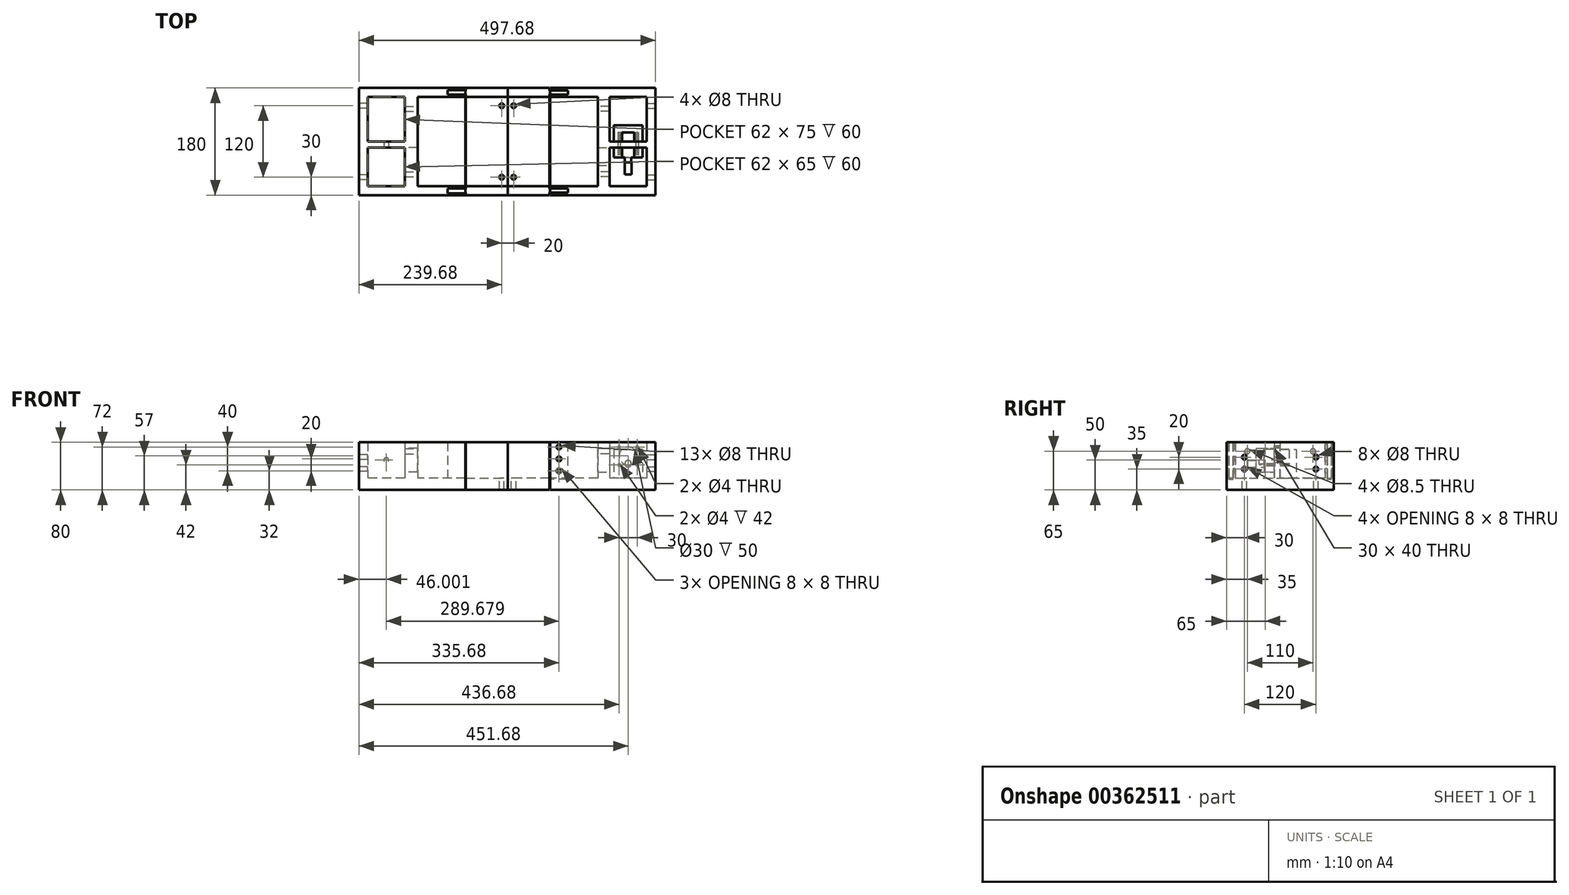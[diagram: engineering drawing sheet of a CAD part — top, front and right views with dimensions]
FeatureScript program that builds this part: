
annotation { "Feature Type Name" : "Feature", "Feature Type Description" : "" }
export const myFeature = defineFeature(function(context is Context, id is Id, definition is map)
    precondition{}
    {
        {
            var Q0;
            Q0=qCreatedBy(makeId("Top.planeOp"),FACE);
            var sketch = newSketch(context, id + "F0", { "sketchPlane" : qUnion([Q0])});
            skLineSegment(sketch, "E0.bottom", {"start": v(24, -27) * mm, "end": v(-24, -27) * mm});
            skLineSegment(sketch, "E0.top", {"start": v(24, 27) * mm, "end": v(-24, 27) * mm});
            skLineSegment(sketch, "E0.left", {"start": v(24, -27) * mm, "end": v(24, 27) * mm});
            skLineSegment(sketch, "E0.right", {"start": v(-24, -27) * mm, "end": v(-24, 27) * mm});
            skPoint(sketch, "E0.middle", {"position": v(0, 0) * mm});
            skSolve(sketch);
        }
        {
            var Q0;
            Q0=makeQuery(id+"F0.imprint","IMPRINT",FACE,{"disambiguationData":[TD([[makeQuery(id+"F0.imprint","IMPRINT",EDGE,{"derivedFrom":sQuery(id+"F0.wireOp",EDGE,"E0.bottom")}),-1.0]])]});
            extrude(context, id + "F1", {"entities" : qUnion([Q0]), "depth" : 48 * mm});
        }
        {
            var Q0;
            Q0=makeQuery(id+"F1.opExtrude","SWEPT_FACE",FACE,{"disambiguationData":[OSD([sQuery(id+"F0.wireOp",EDGE,"E0.bottom")])]});
            var sketch = newSketch(context, id + "F2", { "sketchPlane" : qUnion([Q0])});
            skCircle(sketch, "E1", {"center": v(0, 24) * mm, "radius": 5.5 * mm});
            skPoint(sketch, "E1.centerSnap0", {"position": v(-24, 24) * mm});
            skSolve(sketch);
        }
        {
            var Q0;
            Q0=makeQuery(id+"F2.imprint","IMPRINT",FACE,{"disambiguationData":[TD([[makeQuery(id+"F2.imprint","IMPRINT",EDGE,{"derivedFrom":sQuery(id+"F2.wireOp",EDGE,"E1")}),1.0]])]});
            extrude(context, id + "F3", {"entities" : qUnion([Q0]), "operationType" : NewBodyOperationType.ADD, "depth" : 28 * mm});
        }
        {
            var Q0;
            Q0=qCreatedBy(makeId("Top.planeOp"),FACE);
            var sketch = newSketch(context, id + "F4", { "sketchPlane" : qUnion([Q0])});
            skLineSegment(sketch, "E2.bottom", {"start": v(31, -75) * mm, "end": v(-31, -75) * mm});
            skLineSegment(sketch, "E2.top", {"start": v(31, 75) * mm, "end": v(-31, 75) * mm});
            skLineSegment(sketch, "E2.left", {"start": v(31, -75) * mm, "end": v(31, 75) * mm});
            skLineSegment(sketch, "E2.right", {"start": v(-31, -75) * mm, "end": v(-31, 75) * mm});
            skPoint(sketch, "E2.middle", {"position": v(0, 0) * mm});
            skLineSegment(sketch, "E3.bottom", {"start": v(-31, -75) * mm, "end": v(-51, -75) * mm});
            skLineSegment(sketch, "E3.top", {"start": v(-31, 75) * mm, "end": v(-51, 75) * mm});
            skLineSegment(sketch, "E3.right", {"start": v(-51, -75) * mm, "end": v(-51, 75) * mm});
            skLineSegment(sketch, "E4.bottom", {"start": v(-51, -75) * mm, "end": v(-51, -75) * mm});
            skLineSegment(sketch, "E4.top", {"start": v(-51, 75) * mm, "end": v(-51, 75) * mm});
            skLineSegment(sketch, "E5.bottom", {"start": v(-51, -75) * mm, "end": v(-131, -75) * mm});
            skLineSegment(sketch, "E5.left", {"start": v(-51, -75) * mm, "end": v(-51, 74.37) * mm});
            skLineSegment(sketch, "E6", {"start": v(-51, 75) * mm, "end": v(-131, 75) * mm});
            skLineSegment(sketch, "E7", {"start": v(-131, 75) * mm, "end": v(-131, -75) * mm});
            skLineSegment(sketch, "E8", {"start": v(-131, 75) * mm, "end": v(-131, 90) * mm});
            skLineSegment(sketch, "E9", {"start": v(-131, 90) * mm, "end": v(46, 90) * mm});
            skLineSegment(sketch, "E10", {"start": v(46, 90) * mm, "end": v(46, -90) * mm});
            skLineSegment(sketch, "E11", {"start": v(46, -90) * mm, "end": v(-131, -90) * mm});
            skLineSegment(sketch, "E12", {"start": v(-131, -90) * mm, "end": v(-131, -75) * mm});
            skLineSegment(sketch, "E13.bottom", {"start": v(31, 0) * mm, "end": v(-31, 0) * mm});
            skLineSegment(sketch, "E13.top", {"start": v(31, -10) * mm, "end": v(-31, -10) * mm});
            skLineSegment(sketch, "E13.left", {"start": v(31, 0) * mm, "end": v(31, -10) * mm});
            skLineSegment(sketch, "E13.right", {"start": v(-31, 0) * mm, "end": v(-31, -10) * mm});
            skSolve(sketch);
        }
        {
            var Q0;
            Q0=makeQuery(id+"F4.imprint","IMPRINT",FACE,{"disambiguationData":[TD([[makeQuery(id+"F4.imprint","IMPRINT",EDGE,{"derivedFrom":sQuery(id+"F4.wireOp",EDGE,"E2.bottom")}),1.0]])]});
            var Q1;
            Q1=makeQuery(id+"F4.imprint","IMPRINT",FACE,{"disambiguationData":[TD([[makeQuery(id+"F4.imprint","IMPRINT",EDGE,{"derivedFrom":sQuery(id+"F4.wireOp",EDGE,"E3.bottom")}),-1.0]])]});
            var Q2;
            Q2=makeQuery(id+"F4.imprint","IMPRINT",FACE,{"disambiguationData":[TD([[makeQuery(id+"F4.imprint","IMPRINT",EDGE,{"derivedFrom":sQuery(id+"F4.wireOp",EDGE,"E13.bottom")}),1.0]])]});
            extrude(context, id + "F5", {"entities" : qUnion([Q0, Q1, Q2]), "depth" : 60 * mm});
        }
        {
            var Q0;
            Q0=makeQuery(id+"F5.opExtrude","CAP_FACE",FACE,{"disambiguationData":[OSD([sQuery(id+"F4.wireOp",EDGE,"E2.bottom"),sQuery(id+"F4.wireOp",EDGE,"E2.top"),sQuery(id+"F4.wireOp",EDGE,"E2.left"),sQuery(id+"F4.wireOp",EDGE,"E2.right"),sQuery(id+"F4.wireOp",EDGE,"E3.right"),sQuery(id+"F4.wireOp",EDGE,"E5.bottom"),sQuery(id+"F4.wireOp",EDGE,"E5.left"),sQuery(id+"F4.wireOp",EDGE,"E6"),sQuery(id+"F4.wireOp",EDGE,"E8"),sQuery(id+"F4.wireOp",EDGE,"E9"),sQuery(id+"F4.wireOp",EDGE,"E10"),sQuery(id+"F4.wireOp",EDGE,"E11"),sQuery(id+"F4.wireOp",EDGE,"E12")])],"isStart":true});
            var sketch = newSketch(context, id + "F6", { "sketchPlane" : qUnion([Q0])});
            skLineSegment(sketch, "E14.bottom", {"start": v(46, 90) * mm, "end": v(-131, 90) * mm});
            skLineSegment(sketch, "E14.top", {"start": v(46, -90) * mm, "end": v(-131, -90) * mm});
            skLineSegment(sketch, "E14.left", {"start": v(46, 90) * mm, "end": v(46, -90) * mm});
            skLineSegment(sketch, "E14.right", {"start": v(-131, 90) * mm, "end": v(-131, -90) * mm});
            skSolve(sketch);
        }
        {
            var Q0;
            Q0=makeQuery(id+"F6.imprint","IMPRINT",FACE,{"disambiguationData":[TD([[makeQuery(id+"F6.imprint","IMPRINT",EDGE,{"derivedFrom":makeQuery(id+"F5.opExtrude","CAP_EDGE",EDGE,{"disambiguationData":[OSD([sQuery(id+"F4.wireOp",EDGE,"E2.bottom")])],"isStart":true})}),1.0]])]});
            var Q1;
            {var subQ1=makeQuery(id+"F5.opExtrude","CAP_EDGE",EDGE,{"disambiguationData":[OSD([sQuery(id+"F4.wireOp",EDGE,"E5.bottom")])],"isStart":true});Q1=makeQuery(id+"F6.imprint","IMPRINT",FACE,{"disambiguationData":[TD([[makeQuery(id+"F6.imprint","IMPRINT",EDGE,{"derivedFrom":subQ1}),1.0]])]});}
            var Q2;
            {var subQ10=sQuery(id+"F6.wireOp",EDGE,"E14.bottom");Q2=makeQuery(id+"F6.imprint","IMPRINT",FACE,{"disambiguationData":[TD([[makeQuery(id+"F6.imprint","IMPRINT",EDGE,{"derivedFrom":subQ10}),1.0]])]});}
            var Q3;
            {var subQ0=sQuery(id+"F4.wireOp",EDGE,"E2.top");Q3=makeQuery(id+"F6.imprint","IMPRINT",FACE,{"disambiguationData":[TD([[makeQuery(id+"F6.imprint","IMPRINT",EDGE,{"derivedFrom":makeQuery(id+"F5.opExtrude","CAP_EDGE",EDGE,{"disambiguationData":[OSD([subQ0])],"isStart":true})}),-1.0]])]});}
            extrude(context, id + "F7", {"entities" : qUnion([Q0, Q1, Q2, Q3]), "operationType" : NewBodyOperationType.ADD, "depth" : 20 * mm});
        }
        {
            var Q0;
            Q0=makeQuery(id+"F5.opExtrude","SWEPT_FACE",FACE,{"disambiguationData":[OSD([sQuery(id+"F4.wireOp",EDGE,"E2.right")])]});
            var sketch = newSketch(context, id + "F8", { "sketchPlane" : qUnion([Q0])});
            skLineSegment(sketch, "E15.bottom", {"start": v(-40, 50) * mm, "end": v(-10, 50) * mm});
            skLineSegment(sketch, "E15.top", {"start": v(-40, 10) * mm, "end": v(-10, 10) * mm});
            skLineSegment(sketch, "E15.left", {"start": v(-40, 50) * mm, "end": v(-40, 10) * mm});
            skLineSegment(sketch, "E15.right", {"start": v(-10, 50) * mm, "end": v(-10, 10) * mm});
            skSolve(sketch);
        }
        {
            var Q0;
            Q0 = qSketchRegion(id + "F8", true);
            extrude(context, id + "F9", {"entities" : qUnion([Q0]), "operationType" : NewBodyOperationType.REMOVE, "oppositeDirection" : true, "depth" : 25 * mm});
        }
        {
            var Q0;
            Q0=makeQuery(id+"F9.boolean.opBoolean","MERGE",FACE,{"derivedFrom":[makeQuery(id+"F5.opExtrude","SWEPT_FACE",FACE,{"disambiguationData":[OSD([sQuery(id+"F4.wireOp",EDGE,"E13.top")])]}),makeQuery(id+"F9.opExtrude","SWEPT_FACE",FACE,{"disambiguationData":[OSD([sQuery(id+"F8.wireOp",EDGE,"E15.right")])]})]});
            var sketch = newSketch(context, id + "F10", { "sketchPlane" : qUnion([Q0])});
            skLineSegment(sketch, "E16", {"start": v(0, 60) * mm, "end": v(0, 52) * mm, "construction": true});
            skLineSegment(sketch, "E17", {"start": v(0, 52) * mm, "end": v(15, 52) * mm, "construction": true});
            skLineSegment(sketch, "E18", {"start": v(0, 52) * mm, "end": v(-15, 52) * mm, "construction": true});
            skCircle(sketch, "E19", {"center": v(-15, 52) * mm, "radius": 2 * mm});
            skCircle(sketch, "E20", {"center": v(15, 52) * mm, "radius": 2 * mm});
            skLineSegment(sketch, "E21", {"start": v(-15, 52) * mm, "end": v(-15, 22) * mm, "construction": true});
            skCircle(sketch, "E22", {"center": v(-15, 22) * mm, "radius": 2 * mm});
            skCircle(sketch, "E23", {"center": v(15, 22) * mm, "radius": 2 * mm});
            skLineSegment(sketch, "E24", {"start": v(15, 52) * mm, "end": v(-15, 22) * mm, "construction": true});
            skLineSegment(sketch, "E25", {"start": v(-15, 52) * mm, "end": v(15, 22) * mm, "construction": true});
            skCircle(sketch, "E26", {"center": v(0, 37) * mm, "radius": 15 * mm});
            skSolve(sketch);
        }
        {
            var Q0;
            Q0 = qSketchRegion(id + "F10", true);
            extrude(context, id + "F11", {"entities" : qUnion([Q0]), "operationType" : NewBodyOperationType.REMOVE, "oppositeDirection" : true, "depth" : 25 * mm, "hasSecondDirection" : true, "secondDirectionOppositeDirection" : false, "secondDirectionDepth" : 25 * mm});
        }
        {
            var Q0;
            Q0=makeQuery(id+"F7.boolean.opBoolean","MERGE",FACE,{"derivedFrom":[makeQuery(id+"F5.opExtrude","SWEPT_FACE",FACE,{"disambiguationData":[OSD([sQuery(id+"F4.wireOp",EDGE,"E11")])]}),makeQuery(id+"F7.opExtrude","SWEPT_FACE",FACE,{"disambiguationData":[OSD([sQuery(id+"F6.wireOp",EDGE,"E14.bottom")])]})]});
            var sketch = newSketch(context, id + "F12", { "sketchPlane" : qUnion([Q0])});
            skLineSegment(sketch, "E27", {"start": v(-116, 60) * mm, "end": v(-116, 52) * mm, "construction": true});
            skCircle(sketch, "E28", {"center": v(-116, 52) * mm, "radius": 4 * mm});
            skLineSegment(sketch, "E29", {"start": v(-116, 52) * mm, "end": v(-116, 32) * mm, "construction": true});
            skLineSegment(sketch, "E30", {"start": v(-116, 32) * mm, "end": v(-116, 12) * mm, "construction": true});
            skCircle(sketch, "E31", {"center": v(-116, 32) * mm, "radius": 4 * mm});
            skCircle(sketch, "E32", {"center": v(-116, 12) * mm, "radius": 4 * mm});
            skSolve(sketch);
        }
        {
            var Q0;
            Q0=makeQuery(id+"F7.boolean.opBoolean","MERGE",FACE,{"derivedFrom":[makeQuery(id+"F5.opExtrude","SWEPT_FACE",FACE,{"disambiguationData":[OSD([sQuery(id+"F4.wireOp",EDGE,"E10")])]}),makeQuery(id+"F7.opExtrude","SWEPT_FACE",FACE,{"disambiguationData":[OSD([sQuery(id+"F6.wireOp",EDGE,"E14.left")])]})]});
            var sketch = newSketch(context, id + "F13", { "sketchPlane" : qUnion([Q0])});
            skLineSegment(sketch, "E33", {"start": v(-90, 0) * mm, "end": v(-75, 0) * mm, "construction": true});
            skLineSegment(sketch, "E34", {"start": v(-75, 0) * mm, "end": v(-60, 0) * mm, "construction": true});
            skLineSegment(sketch, "E35", {"start": v(-60, 0) * mm, "end": v(-60, 15) * mm, "construction": true});
            skCircle(sketch, "E36", {"center": v(-60, 15) * mm, "radius": 4 * mm});
            skLineSegment(sketch, "E37", {"start": v(-60, 15) * mm, "end": v(-60, 35) * mm, "construction": true});
            skCircle(sketch, "E38", {"center": v(-60, 35) * mm, "radius": 4 * mm});
            skLineSegment(sketch, "E39", {"start": v(-60, 15) * mm, "end": v(60, 15) * mm, "construction": true});
            skLineSegment(sketch, "E40", {"start": v(90, 15) * mm, "end": v(60, 15) * mm, "construction": true});
            skCircle(sketch, "E41", {"center": v(60, 15) * mm, "radius": 4 * mm});
            skCircle(sketch, "E42", {"center": v(60, 35) * mm, "radius": 4 * mm});
            skSolve(sketch);
        }
        {
            var Q0;
            Q0=makeQuery(id+"F5.opExtrude","CAP_FACE",FACE,{"disambiguationData":[OSD([sQuery(id+"F4.wireOp",EDGE,"E2.bottom"),sQuery(id+"F4.wireOp",EDGE,"E2.top"),sQuery(id+"F4.wireOp",EDGE,"E2.left"),sQuery(id+"F4.wireOp",EDGE,"E2.right"),sQuery(id+"F4.wireOp",EDGE,"E3.right"),sQuery(id+"F4.wireOp",EDGE,"E5.bottom"),sQuery(id+"F4.wireOp",EDGE,"E5.left"),sQuery(id+"F4.wireOp",EDGE,"E6"),sQuery(id+"F4.wireOp",EDGE,"E8"),sQuery(id+"F4.wireOp",EDGE,"E9"),sQuery(id+"F4.wireOp",EDGE,"E10"),sQuery(id+"F4.wireOp",EDGE,"E11"),sQuery(id+"F4.wireOp",EDGE,"E12"),sQuery(id+"F4.wireOp",EDGE,"E13.bottom"),sQuery(id+"F4.wireOp",EDGE,"E13.top")])],"isStart":false});
            var sketch = newSketch(context, id + "F14", { "sketchPlane" : qUnion([Q0])});
            skLineSegment(sketch, "E43", {"start": v(-131, -82.5) * mm, "end": v(-101, -82.5) * mm, "construction": true});
            skPoint(sketch, "E43.endSnap0", {"position": v(-131, -82.5) * mm});
            skLineSegment(sketch, "E44", {"start": v(-101, -82.5) * mm, "end": v(-101, -79) * mm, "construction": true});
            skLineSegment(sketch, "E45", {"start": v(-101, -82.5) * mm, "end": v(-101, -86) * mm, "construction": true});
            skLineSegment(sketch, "E46.bottom", {"start": v(-101, -86) * mm, "end": v(-131, -86) * mm});
            skLineSegment(sketch, "E46.top", {"start": v(-101, -79) * mm, "end": v(-131, -79) * mm});
            skLineSegment(sketch, "E46.left", {"start": v(-101, -86) * mm, "end": v(-101, -79) * mm});
            skLineSegment(sketch, "E46.right", {"start": v(-131, -86) * mm, "end": v(-131, -79) * mm});
            skLineSegment(sketch, "E47.MirrorCS", {"start": v(-101, 86) * mm, "end": v(-131, 86) * mm});
            skLineSegment(sketch, "E48.MirrorCS", {"start": v(-101, 86) * mm, "end": v(-101, 79) * mm});
            skLineSegment(sketch, "E49.MirrorCS", {"start": v(-101, 82.5) * mm, "end": v(-101, 86) * mm, "construction": true});
            skLineSegment(sketch, "E50.MirrorCS", {"start": v(-101, 82.5) * mm, "end": v(-101, 79) * mm, "construction": true});
            skLineSegment(sketch, "E51.MirrorCS", {"start": v(-131, 86) * mm, "end": v(-131, 79) * mm});
            skLineSegment(sketch, "E52.MirrorCS", {"start": v(-101, 79) * mm, "end": v(-131, 79) * mm});
            skLineSegment(sketch, "E53.MirrorCS", {"start": v(-131, 82.5) * mm, "end": v(-101, 82.5) * mm, "construction": true});
            skPoint(sketch, "E54.MirrorP", {"position": v(-131, 82.5) * mm});
            skSolve(sketch);
        }
        {
            var Q0;
            Q0=makeQuery(id+"F13.imprint","IMPRINT",FACE,{"disambiguationData":[TD([[makeQuery(id+"F13.imprint","IMPRINT",EDGE,{"derivedFrom":sQuery(id+"F13.wireOp",EDGE,"E36")}),1.0]])]});
            var Q1;
            Q1=makeQuery(id+"F13.imprint","IMPRINT",FACE,{"disambiguationData":[TD([[makeQuery(id+"F13.imprint","IMPRINT",EDGE,{"derivedFrom":sQuery(id+"F13.wireOp",EDGE,"E38")}),1.0]])]});
            var Q2;
            Q2=makeQuery(id+"F13.imprint","IMPRINT",FACE,{"disambiguationData":[TD([[makeQuery(id+"F13.imprint","IMPRINT",EDGE,{"derivedFrom":sQuery(id+"F13.wireOp",EDGE,"E42")}),1.0]])]});
            var Q3;
            Q3=makeQuery(id+"F13.imprint","IMPRINT",FACE,{"disambiguationData":[TD([[makeQuery(id+"F13.imprint","IMPRINT",EDGE,{"derivedFrom":sQuery(id+"F13.wireOp",EDGE,"E41")}),1.0]])]});
            extrude(context, id + "F15", {"entities" : qUnion([Q0, Q1, Q2, Q3]), "operationType" : NewBodyOperationType.REMOVE, "oppositeDirection" : true, "depth" : 25 * mm});
        }
        {
            var Q0;
            Q0=qCreatedBy(makeId("Top.planeOp"),FACE);
            var sketch = newSketch(context, id + "F16", { "sketchPlane" : qUnion([Q0])});
            skLineSegment(sketch, "E55.bottom", {"start": v(-132, -90) * mm, "end": v(-202, -90) * mm});
            skLineSegment(sketch, "E56", {"start": v(-202, -90) * mm, "end": v(-202, -75) * mm});
            skLineSegment(sketch, "E57", {"start": v(-132, -75) * mm, "end": v(-202, -75) * mm});
            skLineSegment(sketch, "E58", {"start": v(-132, -90) * mm, "end": v(-132, -85.8) * mm});
            skLineSegment(sketch, "E59", {"start": v(-132, -85.8) * mm, "end": v(-103, -85.8) * mm});
            skLineSegment(sketch, "E60", {"start": v(-132, -75) * mm, "end": v(-132, -79.2) * mm});
            skLineSegment(sketch, "E61", {"start": v(-132, -79.2) * mm, "end": v(-103, -79.2) * mm});
            skLineSegment(sketch, "E62", {"start": v(-103, -79.2) * mm, "end": v(-103, -85.8) * mm});
            skSolve(sketch);
        }
        {
            var Q0;
            Q0=makeQuery(id+"F16.imprint","IMPRINT",FACE,{"disambiguationData":[TD([[makeQuery(id+"F16.imprint","IMPRINT",EDGE,{"derivedFrom":sQuery(id+"F16.wireOp",EDGE,"E55.bottom")}),-1.0]])]});
            var Q1;
            Q1=makeQuery(id+"F16.imprint","IMPRINT",FACE,{"disambiguationData":[TD([[makeQuery(id+"F16.imprint","IMPRINT",EDGE,{"derivedFrom":sQuery(id+"F16.wireOp",EDGE,"E55.top")}),1.0]])]});
            extrude(context, id + "F17", {"entities" : qUnion([Q0, Q1]), "depth" : 60 * mm, "hasSecondDirectionDraft" : true, "secondDirectionDraftAngle" : 3 * degree});
        }
        {
            var Q0;
            Q0=makeQuery(id+"F14.imprint","IMPRINT",FACE,{"disambiguationData":[TD([[makeQuery(id+"F14.imprint","IMPRINT",EDGE,{"derivedFrom":sQuery(id+"F14.wireOp",EDGE,"E46.bottom")}),-1.0]])]});
            var Q1;
            Q1=makeQuery(id+"F14.imprint","IMPRINT",FACE,{"disambiguationData":[TD([[makeQuery(id+"F14.imprint","IMPRINT",EDGE,{"derivedFrom":sQuery(id+"F14.wireOp",EDGE,"E48.MirrorCS")}),-1.0]])]});
            extrude(context, id + "F18", {"entities" : qUnion([Q0, Q1]), "operationType" : NewBodyOperationType.REMOVE, "oppositeDirection" : true, "depth" : 62 * mm});
        }
        {
            var Q0;
            Q0=makeQuery(id+"F12.imprint","IMPRINT",FACE,{"disambiguationData":[TD([[makeQuery(id+"F12.imprint","IMPRINT",EDGE,{"derivedFrom":sQuery(id+"F12.wireOp",EDGE,"E32")}),1.0]])]});
            var Q1;
            Q1=makeQuery(id+"F12.imprint","IMPRINT",FACE,{"disambiguationData":[TD([[makeQuery(id+"F12.imprint","IMPRINT",EDGE,{"derivedFrom":sQuery(id+"F12.wireOp",EDGE,"E31")}),1.0]])]});
            var Q2;
            Q2=makeQuery(id+"F12.imprint","IMPRINT",FACE,{"disambiguationData":[TD([[makeQuery(id+"F12.imprint","IMPRINT",EDGE,{"derivedFrom":sQuery(id+"F12.wireOp",EDGE,"E28")}),1.0]])]});
            extrude(context, id + "F19", {"entities" : qUnion([Q0, Q1, Q2]), "operationType" : NewBodyOperationType.REMOVE, "oppositeDirection" : true, "depth" : 300 * mm});
        }
        {
            var Q0;
            Q0=makeQuery(id+"F17.opExtrude","SWEPT_BODY",BODY,{"disambiguationData":[OSD([sQuery(id+"F16.wireOp",EDGE,"E55.bottom"),sQuery(id+"F16.wireOp",EDGE,"E56"),sQuery(id+"F16.wireOp",EDGE,"E57"),sQuery(id+"F16.wireOp",EDGE,"E58"),sQuery(id+"F16.wireOp",EDGE,"E59"),sQuery(id+"F16.wireOp",EDGE,"E60"),sQuery(id+"F16.wireOp",EDGE,"E61"),sQuery(id+"F16.wireOp",EDGE,"E62")])]});
            var Q1;
            Q1=qCreatedBy(makeId("Front.planeOp"),FACE);
            mirror(context, id + "F20", {"entities" : qUnion([Q0]), "mirrorPlane" : qUnion([Q1])});
        }
        {
            var Q0;
            Q0=makeQuery(id+"F17.opExtrude","CAP_FACE",FACE,{"disambiguationData":[OSD([sQuery(id+"F16.wireOp",EDGE,"E55.bottom"),sQuery(id+"F16.wireOp",EDGE,"E56"),sQuery(id+"F16.wireOp",EDGE,"E57"),sQuery(id+"F16.wireOp",EDGE,"E58"),sQuery(id+"F16.wireOp",EDGE,"E59"),sQuery(id+"F16.wireOp",EDGE,"E60"),sQuery(id+"F16.wireOp",EDGE,"E61"),sQuery(id+"F16.wireOp",EDGE,"E62")])],"isStart":true});
            var sketch = newSketch(context, id + "F21", { "sketchPlane" : qUnion([Q0])});
            skLineSegment(sketch, "E63.bottom", {"start": v(-202, 90) * mm, "end": v(-132, 90) * mm});
            skLineSegment(sketch, "E63.right", {"start": v(-132, 90) * mm, "end": v(-132, -90) * mm});
            skLineSegment(sketch, "E64", {"start": v(-132, -90) * mm, "end": v(-202, -90) * mm});
            skLineSegment(sketch, "E65", {"start": v(-202, -90) * mm, "end": v(-202, 90) * mm});
            skSolve(sketch);
        }
        {
            var Q0;
            {var subQ0=sQuery(id+"F21.wireOp",EDGE,"E63.top");Q0=makeQuery(id+"F21.imprint","IMPRINT",FACE,{"disambiguationData":[TD([[makeQuery(id+"F21.imprint","IMPRINT",EDGE,{"derivedFrom":subQ0}),1.0]])]});}
            var Q1;
            {var subQ5=sQuery(id+"F21.wireOp",EDGE,"E63.bottom");Q1=makeQuery(id+"F21.imprint","IMPRINT",FACE,{"disambiguationData":[TD([[makeQuery(id+"F21.imprint","IMPRINT",EDGE,{"derivedFrom":subQ5}),1.0]])]});}
            var Q2;
            {var subQ2=sQuery(id+"F21.wireOp",EDGE,"E64");Q2=makeQuery(id+"F21.imprint","IMPRINT",FACE,{"disambiguationData":[TD([[makeQuery(id+"F21.imprint","IMPRINT",EDGE,{"derivedFrom":subQ2}),-1.0]])]});}
            extrude(context, id + "F22", {"entities" : qUnion([Q0, Q1, Q2]), "operationType" : NewBodyOperationType.ADD, "depth" : 20 * mm});
        }
        {
            var Q0;
            Q0=makeQuery(id+"F17.opExtrude","SWEPT_BODY",BODY,{"disambiguationData":[OSD([sQuery(id+"F16.wireOp",EDGE,"E55.bottom"),sQuery(id+"F16.wireOp",EDGE,"E56"),sQuery(id+"F16.wireOp",EDGE,"E57"),sQuery(id+"F16.wireOp",EDGE,"E58"),sQuery(id+"F16.wireOp",EDGE,"E59"),sQuery(id+"F16.wireOp",EDGE,"E60"),sQuery(id+"F16.wireOp",EDGE,"E61"),sQuery(id+"F16.wireOp",EDGE,"E62")])]});
            var Q1;
            {var subQ0=sQuery(id+"F16.wireOp",EDGE,"E56");var subQ1=makeQuery(id+"F17.opExtrude","SWEPT_FACE",FACE,{"disambiguationData":[OSD([subQ0])]});Q1=makeQuery(id+"F22.boolean.opBoolean","MERGE",FACE,{"derivedFrom":[subQ1,makeQuery(id+"F20.opPattern","COPY",FACE,{"derivedFrom":subQ1,"instanceName":"1"}),makeQuery(id+"F22.opExtrude","SWEPT_FACE",FACE,{"disambiguationData":[OSD([subQ0])]}),makeQuery(id+"F22.opExtrude","SWEPT_FACE",FACE,{"disambiguationData":[OSD([sQuery(id+"F21.wireOp",EDGE,"E65")])]})]});}
            mirror(context, id + "F23", {"operationType" : NewBodyOperationType.ADD, "entities" : qUnion([Q0]), "mirrorPlane" : qUnion([Q1])});
        }
        {
            var Q0;
            Q0=qCreatedBy(makeId("Top.planeOp"),FACE);
            var sketch = newSketch(context, id + "F24", { "sketchPlane" : qUnion([Q0])});
            skLineSegment(sketch, "E66.bottom", {"start": v(-273, -90) * mm, "end": v(-353, -90) * mm});
            skLineSegment(sketch, "E66.top", {"start": v(-273, 90) * mm, "end": v(-353, 90) * mm});
            skLineSegment(sketch, "E67.bottom", {"start": v(-273, -75) * mm, "end": v(-353, -75) * mm});
            skLineSegment(sketch, "E67.top", {"start": v(-273, 75) * mm, "end": v(-353, 75) * mm});
            skLineSegment(sketch, "E67.left", {"start": v(-273, -75) * mm, "end": v(-273, 75) * mm});
            skLineSegment(sketch, "E68.bottom", {"start": v(-353, -90) * mm, "end": v(-374.68, -90) * mm});
            skLineSegment(sketch, "E68.top", {"start": v(-353, 90) * mm, "end": v(-374.68, 90) * mm});
            skLineSegment(sketch, "E69.bottom", {"start": v(-374.68, -90) * mm, "end": v(-436.68, -90) * mm});
            skLineSegment(sketch, "E69.top", {"start": v(-374.68, 90) * mm, "end": v(-436.68, 90) * mm});
            skLineSegment(sketch, "E70.bottom", {"start": v(-436.68, -90) * mm, "end": v(-451.68, -90) * mm});
            skLineSegment(sketch, "E70.top", {"start": v(-436.68, 90) * mm, "end": v(-451.68, 90) * mm});
            skLineSegment(sketch, "E70.right", {"start": v(-451.68, -90) * mm, "end": v(-451.68, 90) * mm});
            skLineSegment(sketch, "E71", {"start": v(-353, -75) * mm, "end": v(-374.68, -75) * mm});
            skLineSegment(sketch, "E72", {"start": v(-353, 75) * mm, "end": v(-374.68, 75) * mm});
            skLineSegment(sketch, "E73", {"start": v(-374.68, -75) * mm, "end": v(-436.68, -75) * mm});
            skLineSegment(sketch, "E74", {"start": v(-374.68, 75) * mm, "end": v(-436.68, 75) * mm});
            skLineSegment(sketch, "E75", {"start": v(-436.68, 75) * mm, "end": v(-436.68, -75) * mm});
            skLineSegment(sketch, "E76", {"start": v(-374.68, -75) * mm, "end": v(-374.68, 75) * mm});
            skLineSegment(sketch, "E77", {"start": v(-353, 75) * mm, "end": v(-353, -75) * mm});
            skLineSegment(sketch, "E78", {"start": v(-374.68, 0) * mm, "end": v(-436.68, 0) * mm});
            skPoint(sketch, "E78.startSnap0", {"position": v(-374.68, 0) * mm});
            skLineSegment(sketch, "E79", {"start": v(-436.68, 0) * mm, "end": v(-436.68, -10) * mm});
            skLineSegment(sketch, "E80", {"start": v(-436.68, -10) * mm, "end": v(-374.68, -10) * mm});
            skLineSegment(sketch, "E81", {"start": v(-374.68, -10) * mm, "end": v(-374.68, 0) * mm});
            skLineSegment(sketch, "E82", {"start": v(-273, -90) * mm, "end": v(-273, -87) * mm});
            skLineSegment(sketch, "E83", {"start": v(-273, -87) * mm, "end": v(-303, -87) * mm});
            skLineSegment(sketch, "E84", {"start": v(-273, -75) * mm, "end": v(-273, -78.5) * mm});
            skLineSegment(sketch, "E85", {"start": v(-273, -78.5) * mm, "end": v(-303, -78.5) * mm});
            skLineSegment(sketch, "E86", {"start": v(-303, -78.5) * mm, "end": v(-303, -87) * mm});
            skLineSegment(sketch, "E87", {"start": v(-273, 90) * mm, "end": v(-273, 86.5) * mm});
            skLineSegment(sketch, "E88", {"start": v(-273, 86.5) * mm, "end": v(-303, 86.5) * mm});
            skLineSegment(sketch, "E89", {"start": v(-273, 75) * mm, "end": v(-273, 78.5) * mm});
            skLineSegment(sketch, "E90", {"start": v(-273, 78.5) * mm, "end": v(-303, 78.5) * mm});
            skLineSegment(sketch, "E91", {"start": v(-303, 78.5) * mm, "end": v(-303, 86.5) * mm});
            skSolve(sketch);
        }
        {
            var Q0;
            {var subQ2=sQuery(id+"F24.wireOp",EDGE,"E66.bottom");Q0=makeQuery(id+"F24.imprint","IMPRINT",FACE,{"disambiguationData":[TD([[makeQuery(id+"F24.imprint","IMPRINT",EDGE,{"derivedFrom":subQ2}),-1.0]])]});}
            var Q1;
            {var subQ3=sQuery(id+"F24.wireOp",EDGE,"E71");Q1=makeQuery(id+"F24.imprint","IMPRINT",FACE,{"disambiguationData":[TD([[makeQuery(id+"F24.imprint","IMPRINT",EDGE,{"derivedFrom":subQ3}),-1.0]])]});}
            var Q2;
            Q2=makeQuery(id+"F24.imprint","IMPRINT",FACE,{"disambiguationData":[TD([[makeQuery(id+"F24.imprint","IMPRINT",EDGE,{"derivedFrom":sQuery(id+"F24.wireOp",EDGE,"E78")}),1.0]])]});
            extrude(context, id + "F25", {"entities" : qUnion([Q0, Q1, Q2]), "operationType" : NewBodyOperationType.ADD, "depth" : 60 * mm});
        }
        {
            var Q0;
            Q0=makeQuery(id+"F25.opExtrude","CAP_FACE",FACE,{"disambiguationData":[OSD([sQuery(id+"F24.wireOp",EDGE,"E66.bottom"),sQuery(id+"F24.wireOp",EDGE,"E66.top"),sQuery(id+"F24.wireOp",EDGE,"E67.bottom"),sQuery(id+"F24.wireOp",EDGE,"E67.top"),sQuery(id+"F24.wireOp",EDGE,"E68.bottom"),sQuery(id+"F24.wireOp",EDGE,"E68.top"),sQuery(id+"F24.wireOp",EDGE,"E69.bottom"),sQuery(id+"F24.wireOp",EDGE,"E69.top"),sQuery(id+"F24.wireOp",EDGE,"E70.bottom"),sQuery(id+"F24.wireOp",EDGE,"E70.top"),sQuery(id+"F24.wireOp",EDGE,"E70.right"),sQuery(id+"F24.wireOp",EDGE,"E73"),sQuery(id+"F24.wireOp",EDGE,"E74"),sQuery(id+"F24.wireOp",EDGE,"E75"),sQuery(id+"F24.wireOp",EDGE,"E76"),sQuery(id+"F24.wireOp",EDGE,"E77"),sQuery(id+"F24.wireOp",EDGE,"E78"),sQuery(id+"F24.wireOp",EDGE,"E80"),sQuery(id+"F24.wireOp",EDGE,"E82"),sQuery(id+"F24.wireOp",EDGE,"E83"),sQuery(id+"F24.wireOp",EDGE,"E84"),sQuery(id+"F24.wireOp",EDGE,"E85"),sQuery(id+"F24.wireOp",EDGE,"E86"),sQuery(id+"F24.wireOp",EDGE,"E87"),sQuery(id+"F24.wireOp",EDGE,"E88"),sQuery(id+"F24.wireOp",EDGE,"E89"),sQuery(id+"F24.wireOp",EDGE,"E90"),sQuery(id+"F24.wireOp",EDGE,"E91")])],"isStart":true});
            var sketch = newSketch(context, id + "F26", { "sketchPlane" : qUnion([Q0])});
            skLineSegment(sketch, "E92.bottom", {"start": v(-451.68, -90) * mm, "end": v(-273, -90) * mm});
            skLineSegment(sketch, "E92.top", {"start": v(-451.68, 87) * mm, "end": v(-273, 87) * mm});
            skLineSegment(sketch, "E92.left", {"start": v(-451.68, -90) * mm, "end": v(-451.68, 87) * mm});
            skLineSegment(sketch, "E92.right", {"start": v(-273, -90) * mm, "end": v(-273, 87) * mm});
            skSolve(sketch);
        }
        {
            var Q0;
            {var subQ6=sQuery(id+"F26.wireOp",EDGE,"E92.bottom");Q0=makeQuery(id+"F26.imprint","IMPRINT",FACE,{"disambiguationData":[TD([[makeQuery(id+"F26.imprint","IMPRINT",EDGE,{"derivedFrom":subQ6}),-1.0]])]});}
            var Q1;
            {var subQ4=makeQuery(id+"F25.opExtrude","CAP_EDGE",EDGE,{"disambiguationData":[OSD([sQuery(id+"F24.wireOp",EDGE,"E82")])],"isStart":true});Q1=makeQuery(id+"F26.imprint","IMPRINT",FACE,{"disambiguationData":[TD([[makeQuery(id+"F26.imprint","IMPRINT",EDGE,{"derivedFrom":subQ4}),-1.0]])]});}
            var Q2;
            {var subQ0=sQuery(id+"F24.wireOp",EDGE,"E74");Q2=makeQuery(id+"F26.imprint","IMPRINT",FACE,{"disambiguationData":[TD([[makeQuery(id+"F26.imprint","IMPRINT",EDGE,{"derivedFrom":makeQuery(id+"F25.opExtrude","CAP_EDGE",EDGE,{"disambiguationData":[OSD([subQ0])],"isStart":true})}),-1.0]])]});}
            var Q3;
            {var subQ0=sQuery(id+"F24.wireOp",EDGE,"E73");Q3=makeQuery(id+"F26.imprint","IMPRINT",FACE,{"disambiguationData":[TD([[makeQuery(id+"F26.imprint","IMPRINT",EDGE,{"derivedFrom":makeQuery(id+"F25.opExtrude","CAP_EDGE",EDGE,{"disambiguationData":[OSD([subQ0])],"isStart":true})}),1.0]])]});}
            var Q4;
            {var subQ1=makeQuery(id+"F25.opExtrude","CAP_EDGE",EDGE,{"disambiguationData":[OSD([sQuery(id+"F24.wireOp",EDGE,"E67.bottom")])],"isStart":true});Q4=makeQuery(id+"F26.imprint","IMPRINT",FACE,{"disambiguationData":[TD([[makeQuery(id+"F26.imprint","IMPRINT",EDGE,{"derivedFrom":subQ1}),1.0]])]});}
            var Q5;
            {var subQ4=makeQuery(id+"F25.opExtrude","CAP_EDGE",EDGE,{"disambiguationData":[OSD([sQuery(id+"F24.wireOp",EDGE,"E85")])],"isStart":true});Q5=makeQuery(id+"F26.imprint","IMPRINT",FACE,{"disambiguationData":[TD([[makeQuery(id+"F26.imprint","IMPRINT",EDGE,{"derivedFrom":subQ4}),-1.0]])]});}
            var Q6;
            {var subQ1=makeQuery(id+"F25.opExtrude","CAP_EDGE",EDGE,{"disambiguationData":[OSD([sQuery(id+"F24.wireOp",EDGE,"E88")])],"isStart":true});Q6=makeQuery(id+"F26.imprint","IMPRINT",FACE,{"disambiguationData":[TD([[makeQuery(id+"F26.imprint","IMPRINT",EDGE,{"derivedFrom":subQ1}),-1.0]])]});}
            extrude(context, id + "F27", {"entities" : qUnion([Q0, Q1, Q2, Q3, Q4, Q5, Q6]), "operationType" : NewBodyOperationType.ADD, "depth" : 20 * mm});
        }
        {
            var Q0;
            Q0=makeQuery(id+"F25.opExtrude","SWEPT_FACE",FACE,{"disambiguationData":[OSD([sQuery(id+"F24.wireOp",EDGE,"E80")])]});
            var sketch = newSketch(context, id + "F28", { "sketchPlane" : qUnion([Q0])});
            skCircle(sketch, "E93", {"center": v(-405.68, 30) * mm, "radius": 4 * mm});
            skPoint(sketch, "E93.centerSnap0", {"position": v(-374.68, 30) * mm});
            skPoint(sketch, "E93.centerSnap1", {"position": v(-405.68, 0) * mm});
            skSolve(sketch);
        }
        {
            var Q0;
            Q0=makeQuery(id+"F28.imprint","IMPRINT",FACE,{"disambiguationData":[TD([[makeQuery(id+"F28.imprint","IMPRINT",EDGE,{"derivedFrom":sQuery(id+"F28.wireOp",EDGE,"E93")}),1.0]])]});
            extrude(context, id + "F29", {"entities" : qUnion([Q0]), "operationType" : NewBodyOperationType.REMOVE, "oppositeDirection" : true, "depth" : 25 * mm});
        }
        {
            var Q0;
            {var subQ0=sQuery(id+"F24.wireOp",EDGE,"E76");Q0=makeQuery(id+"F25.opExtrude","SWEPT_FACE",FACE,{"disambiguationData":[OSD([subQ0]),TDD([makeQuery(id+"F24.imprint","IMPRINT",EDGE,{"disambiguationData":[TD([[makeQuery(id+"F24.imprint","INTERSECT",VERTEX,{"derivedFrom":[sQuery(id+"F24.wireOp",EDGE,"E71"),sQuery(id+"F24.wireOp",EDGE,"E73"),subQ0]}),-1.0]])],"derivedFrom":subQ0})])]});}
            var sketch = newSketch(context, id + "F30", { "sketchPlane" : qUnion([Q0])});
            skLineSegment(sketch, "E94", {"start": v(10, 60) * mm, "end": v(10, 50) * mm, "construction": true});
            skLineSegment(sketch, "E95.bottom", {"start": v(10, 50) * mm, "end": v(40, 50) * mm});
            skLineSegment(sketch, "E95.top", {"start": v(10, 10) * mm, "end": v(40, 10) * mm});
            skLineSegment(sketch, "E95.left", {"start": v(10, 50) * mm, "end": v(10, 10) * mm});
            skLineSegment(sketch, "E95.right", {"start": v(40, 50) * mm, "end": v(40, 10) * mm});
            skSolve(sketch);
        }
        {
            var Q0;
            Q0=makeQuery(id+"F30.imprint","IMPRINT",FACE,{"disambiguationData":[TD([[makeQuery(id+"F30.imprint","IMPRINT",EDGE,{"derivedFrom":sQuery(id+"F30.wireOp",EDGE,"E95.bottom")}),-1.0]])]});
            extrude(context, id + "F31", {"entities" : qUnion([Q0]), "operationType" : NewBodyOperationType.REMOVE, "oppositeDirection" : true, "depth" : 25 * mm});
        }
        {
            var Q0;
            {var subQ0=sQuery(id+"F24.wireOp",EDGE,"E70.right");Q0=makeQuery(id+"F27.boolean.opBoolean","MERGE",FACE,{"derivedFrom":[makeQuery(id+"F25.opExtrude","SWEPT_FACE",FACE,{"disambiguationData":[OSD([subQ0])]}),makeQuery(id+"F27.opExtrude","SWEPT_FACE",FACE,{"disambiguationData":[OSD([subQ0,sQuery(id+"F26.wireOp",EDGE,"E92.left")])]})]});}
            var sketch = newSketch(context, id + "F32", { "sketchPlane" : qUnion([Q0])});
            skLineSegment(sketch, "E96", {"start": v(60, 0) * mm, "end": v(60, 15) * mm, "construction": true});
            skLineSegment(sketch, "E97", {"start": v(60, 15) * mm, "end": v(90, 15) * mm, "construction": true});
            skLineSegment(sketch, "E98", {"start": v(60, 15) * mm, "end": v(60, 35) * mm, "construction": true});
            skLineSegment(sketch, "E99", {"start": v(60, 15) * mm, "end": v(-60, 15) * mm, "construction": true});
            skLineSegment(sketch, "E100", {"start": v(-60, 15) * mm, "end": v(-60, 35) * mm, "construction": true});
            skCircle(sketch, "E101", {"center": v(-60, 35) * mm, "radius": 4 * mm});
            skCircle(sketch, "E102", {"center": v(-60, 15) * mm, "radius": 4 * mm});
            skCircle(sketch, "E103", {"center": v(60, 15) * mm, "radius": 4 * mm});
            skCircle(sketch, "E104", {"center": v(60, 35) * mm, "radius": 4 * mm});
            skSolve(sketch);
        }
        {
            var Q0;
            Q0=makeQuery(id+"F32.imprint","IMPRINT",FACE,{"disambiguationData":[TD([[makeQuery(id+"F32.imprint","IMPRINT",EDGE,{"derivedFrom":sQuery(id+"F32.wireOp",EDGE,"E104")}),1.0]])]});
            var Q1;
            Q1=makeQuery(id+"F32.imprint","IMPRINT",FACE,{"disambiguationData":[TD([[makeQuery(id+"F32.imprint","IMPRINT",EDGE,{"derivedFrom":sQuery(id+"F32.wireOp",EDGE,"E103")}),1.0]])]});
            var Q2;
            Q2=makeQuery(id+"F32.imprint","IMPRINT",FACE,{"disambiguationData":[TD([[makeQuery(id+"F32.imprint","IMPRINT",EDGE,{"derivedFrom":sQuery(id+"F32.wireOp",EDGE,"E101")}),1.0]])]});
            var Q3;
            Q3=makeQuery(id+"F32.imprint","IMPRINT",FACE,{"disambiguationData":[TD([[makeQuery(id+"F32.imprint","IMPRINT",EDGE,{"derivedFrom":sQuery(id+"F32.wireOp",EDGE,"E102")}),1.0]])]});
            extrude(context, id + "F33", {"entities" : qUnion([Q0, Q1, Q2, Q3]), "operationType" : NewBodyOperationType.REMOVE, "oppositeDirection" : true, "depth" : 25 * mm});
        }
        {
            var Q0;
            Q0=makeQuery(id+"F25.opExtrude","SWEPT_FACE",FACE,{"disambiguationData":[OSD([sQuery(id+"F24.wireOp",EDGE,"E77")])]});
            var sketch = newSketch(context, id + "F34", { "sketchPlane" : qUnion([Q0])});
            skLineSegment(sketch, "E105.bottom", {"start": v(-75, 60) * mm, "end": v(-55, 60) * mm, "construction": true});
            skLineSegment(sketch, "E105.top", {"start": v(-75, 45) * mm, "end": v(-55, 45) * mm, "construction": true});
            skLineSegment(sketch, "E105.left", {"start": v(-75, 60) * mm, "end": v(-75, 45) * mm, "construction": true});
            skLineSegment(sketch, "E105.right", {"start": v(-55, 60) * mm, "end": v(-55, 45) * mm, "construction": true});
            skLineSegment(sketch, "E106.bottom", {"start": v(75, 60) * mm, "end": v(55, 60) * mm, "construction": true});
            skLineSegment(sketch, "E106.top", {"start": v(75, 45) * mm, "end": v(55, 45) * mm, "construction": true});
            skLineSegment(sketch, "E106.left", {"start": v(75, 60) * mm, "end": v(75, 45) * mm, "construction": true});
            skLineSegment(sketch, "E106.right", {"start": v(55, 60) * mm, "end": v(55, 45) * mm, "construction": true});
            skCircle(sketch, "E107", {"center": v(-55, 45) * mm, "radius": 4.25 * mm});
            skCircle(sketch, "E108", {"center": v(55, 45) * mm, "radius": 4.25 * mm});
            skSolve(sketch);
        }
        {
            var Q0;
            Q0=makeQuery(id+"F34.imprint","IMPRINT",FACE,{"disambiguationData":[TD([[makeQuery(id+"F34.imprint","IMPRINT",EDGE,{"derivedFrom":sQuery(id+"F34.wireOp",EDGE,"E108")}),1.0]])]});
            var Q1;
            Q1=makeQuery(id+"F34.imprint","IMPRINT",FACE,{"disambiguationData":[TD([[makeQuery(id+"F34.imprint","IMPRINT",EDGE,{"derivedFrom":sQuery(id+"F34.wireOp",EDGE,"E107")}),1.0]])]});
            extrude(context, id + "F35", {"entities" : qUnion([Q0, Q1]), "operationType" : NewBodyOperationType.REMOVE, "oppositeDirection" : true, "depth" : 25 * mm});
        }
        {
            var Q0;
            Q0=makeQuery(id+"F5.opExtrude","SWEPT_FACE",FACE,{"disambiguationData":[OSD([sQuery(id+"F4.wireOp",EDGE,"E3.right"),sQuery(id+"F4.wireOp",EDGE,"E5.left")])]});
            var sketch = newSketch(context, id + "F36", { "sketchPlane" : qUnion([Q0])});
            skLineSegment(sketch, "E109.bottom", {"start": v(-75, 60) * mm, "end": v(-55, 60) * mm, "construction": true});
            skLineSegment(sketch, "E109.top", {"start": v(-75, 45) * mm, "end": v(-55, 45) * mm, "construction": true});
            skLineSegment(sketch, "E109.left", {"start": v(-75, 60) * mm, "end": v(-75, 45) * mm, "construction": true});
            skLineSegment(sketch, "E109.right", {"start": v(-55, 60) * mm, "end": v(-55, 45) * mm, "construction": true});
            skLineSegment(sketch, "E110.bottom", {"start": v(75, 60) * mm, "end": v(55, 60) * mm, "construction": true});
            skLineSegment(sketch, "E110.top", {"start": v(75, 45) * mm, "end": v(55, 45) * mm, "construction": true});
            skLineSegment(sketch, "E110.left", {"start": v(75, 60) * mm, "end": v(75, 45) * mm, "construction": true});
            skLineSegment(sketch, "E110.right", {"start": v(55, 60) * mm, "end": v(55, 45) * mm, "construction": true});
            skCircle(sketch, "E111", {"center": v(55, 45) * mm, "radius": 4.25 * mm});
            skCircle(sketch, "E112", {"center": v(-55, 45) * mm, "radius": 4.25 * mm});
            skSolve(sketch);
        }
        {
            var Q0;
            Q0=makeQuery(id+"F36.imprint","IMPRINT",FACE,{"disambiguationData":[TD([[makeQuery(id+"F36.imprint","IMPRINT",EDGE,{"derivedFrom":sQuery(id+"F36.wireOp",EDGE,"E111")}),1.0]])]});
            var Q1;
            Q1=makeQuery(id+"F36.imprint","IMPRINT",FACE,{"disambiguationData":[TD([[makeQuery(id+"F36.imprint","IMPRINT",EDGE,{"derivedFrom":sQuery(id+"F36.wireOp",EDGE,"E112")}),1.0]])]});
            extrude(context, id + "F37", {"entities" : qUnion([Q0, Q1]), "operationType" : NewBodyOperationType.REMOVE, "oppositeDirection" : true, "depth" : 25 * mm});
        }
        {
            var Q0;
            {var subQ0=makeQuery(id+"F22.opExtrude","CAP_FACE",FACE,{"disambiguationData":[OSD([sQuery(id+"F21.wireOp",EDGE,"E63.bottom"),sQuery(id+"F21.wireOp",EDGE,"E63.right"),sQuery(id+"F21.wireOp",EDGE,"E64"),sQuery(id+"F21.wireOp",EDGE,"E65")])],"isStart":true});Q0=makeQuery(id+"F23.boolean.opBoolean","MERGE",FACE,{"derivedFrom":[subQ0,makeQuery(id+"F23.opPattern","COPY",FACE,{"derivedFrom":subQ0,"instanceName":"1"})]});}
            var sketch = newSketch(context, id + "F38", { "sketchPlane" : qUnion([Q0])});
            skPoint(sketch, "E113.startSnap0", {"position": v(-202, 75) * mm});
            skPoint(sketch, "E113.endSnap0", {"position": v(-202, 75) * mm});
            skLineSegment(sketch, "E114", {"start": v(-202, 0) * mm, "end": v(-202, 60) * mm, "construction": true});
            skLineSegment(sketch, "E115", {"start": v(-202, 0) * mm, "end": v(-202, -60) * mm, "construction": true});
            skLineSegment(sketch, "E116", {"start": v(-202, 60) * mm, "end": v(-212, 60) * mm, "construction": true});
            skLineSegment(sketch, "E117", {"start": v(-202, -60) * mm, "end": v(-192, -60) * mm, "construction": true});
            skCircle(sketch, "E118", {"center": v(-192, -60) * mm, "radius": 4 * mm});
            skCircle(sketch, "E119", {"center": v(-212, 60) * mm, "radius": 4 * mm});
            skCircle(sketch, "E120", {"center": v(-192, 60) * mm, "radius": 4 * mm});
            skCircle(sketch, "E121", {"center": v(-212, -60) * mm, "radius": 4 * mm});
            skSolve(sketch);
        }
        {
            var Q0;
            Q0=makeQuery(id+"F38.imprint","IMPRINT",FACE,{"disambiguationData":[TD([[makeQuery(id+"F38.imprint","IMPRINT",EDGE,{"derivedFrom":sQuery(id+"F38.wireOp",EDGE,"E119")}),1.0]])]});
            var Q1;
            Q1=makeQuery(id+"F38.imprint","IMPRINT",FACE,{"disambiguationData":[TD([[makeQuery(id+"F38.imprint","IMPRINT",EDGE,{"derivedFrom":sQuery(id+"F38.wireOp",EDGE,"E118")}),1.0]])]});
            var Q2;
            Q2=makeQuery(id+"F38.imprint","IMPRINT",FACE,{"disambiguationData":[TD([[makeQuery(id+"F38.imprint","IMPRINT",EDGE,{"derivedFrom":sQuery(id+"F38.wireOp",EDGE,"E121")}),1.0]])]});
            var Q3;
            Q3=makeQuery(id+"F38.imprint","IMPRINT",FACE,{"disambiguationData":[TD([[makeQuery(id+"F38.imprint","IMPRINT",EDGE,{"derivedFrom":sQuery(id+"F38.wireOp",EDGE,"E120")}),1.0]])]});
            extrude(context, id + "F39", {"entities" : qUnion([Q0, Q1, Q2, Q3]), "operationType" : NewBodyOperationType.REMOVE, "oppositeDirection" : true, "depth" : 25 * mm});
        }
    });
